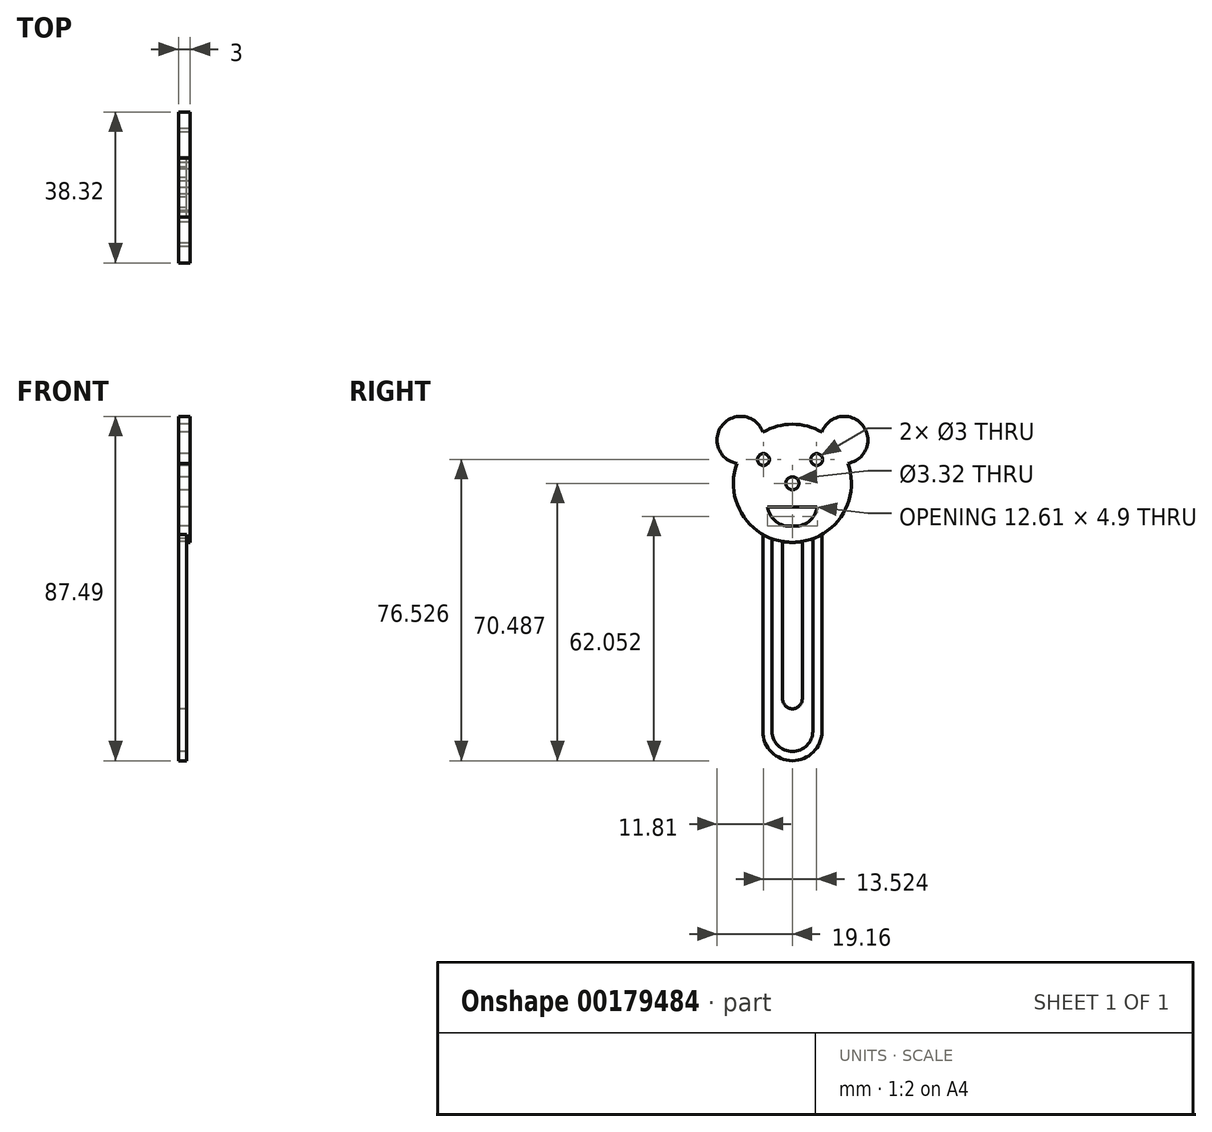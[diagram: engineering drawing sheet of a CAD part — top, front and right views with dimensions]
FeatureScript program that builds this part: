
annotation { "Feature Type Name" : "Feature", "Feature Type Description" : "" }
export const myFeature = defineFeature(function(context is Context, id is Id, definition is map)
    precondition{}
    {
        {
            var Q0;
            Q0=qCreatedBy(makeId("Right.planeOp"),FACE);
            var sketch = newSketch(context, id + "F0", { "sketchPlane" : qUnion([Q0])});
            skCircle(sketch, "E0", {"center": v(0, 41.87) * mm, "radius": 15 * mm});
            skCircle(sketch, "E1", {"center": v(-7.35, 47.9) * mm, "radius": 1.5 * mm});
            skCircle(sketch, "E2", {"center": v(6.17, 47.9) * mm, "radius": 1.5 * mm});
            skCircle(sketch, "E3", {"center": v(0, 41.87) * mm, "radius": 1.66 * mm});
            skArc(sketch, "E4", {"start": v(-8.37, 54.31) * mm, "mid": v(-17, 56.08) * mm, "end": v(-13.73, 47.9) * mm});
            skArc(sketch, "E5", {"start": v(13.73, 47.9) * mm, "mid": v(17, 56.08) * mm, "end": v(8.37, 54.31) * mm});
            skLineSegment(sketch, "E6", {"start": v(-7.5, 28.88) * mm, "end": v(-7.5, -21.12) * mm});
            skLineSegment(sketch, "E7", {"start": v(8.37, 54.31) * mm, "end": v(-40.5, 54.31) * mm, "construction": true});
            skArc(sketch, "E8.0", {"start": v(-7.5, 54.86) * mm, "mid": v(-17.76, 56.72) * mm, "end": v(-14.11, 46.95) * mm});
            skArc(sketch, "E9.0", {"start": v(14.11, 46.95) * mm, "mid": v(17.76, 56.72) * mm, "end": v(7.5, 54.86) * mm});
            skLineSegment(sketch, "E10.MirrorCS", {"start": v(7.5, 28.88) * mm, "end": v(7.5, -21.12) * mm});
            skLineSegment(sketch, "E11.0", {"start": v(-2.5, 27.08) * mm, "end": v(-2.5, -12.92) * mm});
            skLineSegment(sketch, "E12.MirrorCS", {"start": v(2.5, 27.08) * mm, "end": v(2.5, -12.92) * mm});
            skLineSegment(sketch, "E13", {"start": v(0, 35.88) * mm, "end": v(-6.3, 35.88) * mm});
            skArc(sketch, "E14", {"start": v(-6.3, 35.88) * mm, "mid": v(-4.16, 32.15) * mm, "end": v(0, 31.01) * mm});
            skLineSegment(sketch, "E15.MirrorCS", {"start": v(0, 35.88) * mm, "end": v(6.3, 35.88) * mm});
            skArc(sketch, "E16.MirrorCS", {"start": v(6.3, 35.88) * mm, "mid": v(4.16, 32.15) * mm, "end": v(0, 31.01) * mm});
            skArc(sketch, "E17", {"start": v(-2.5, -12.92) * mm, "mid": v(0, -15.42) * mm, "end": v(2.5, -12.92) * mm});
            skLineSegment(sketch, "E18", {"start": v(-5.16, 27.78) * mm, "end": v(-5.16, -21.12) * mm});
            skLineSegment(sketch, "E19.MirrorCS", {"start": v(5.16, 27.78) * mm, "end": v(5.16, -21.12) * mm});
            skArc(sketch, "E20", {"start": v(-5.16, -21.12) * mm, "mid": v(0, -26.28) * mm, "end": v(5.16, -21.12) * mm});
            skArc(sketch, "E21", {"start": v(-7.5, -21.12) * mm, "mid": v(0, -28.62) * mm, "end": v(7.5, -21.12) * mm});
            skSolve(sketch);
        }
        {
            var Q0;
            Q0=makeQuery(id+"F0.imprint","IMPRINT",FACE,{"disambiguationData":[TD([[makeQuery(id+"F0.imprint","IMPRINT",EDGE,{"derivedFrom":sQuery(id+"F0.wireOp",EDGE,"E1")}),-1.0]])]});
            var Q1;
            {var subQ0=sQuery(id+"F0.wireOp",EDGE,"E5");Q1=makeQuery(id+"F0.imprint","IMPRINT",FACE,{"disambiguationData":[TD([[makeQuery(id+"F0.imprint","IMPRINT",EDGE,{"derivedFrom":subQ0}),1.0]])]});}
            var Q2;
            {var subQ0=sQuery(id+"F0.wireOp",EDGE,"E4");Q2=makeQuery(id+"F0.imprint","IMPRINT",FACE,{"disambiguationData":[TD([[makeQuery(id+"F0.imprint","IMPRINT",EDGE,{"derivedFrom":subQ0}),1.0]])]});}
            var Q3;
            {var subQ0=sQuery(id+"F0.wireOp",EDGE,"E5");Q3=makeQuery(id+"F0.imprint","IMPRINT",FACE,{"disambiguationData":[TD([[makeQuery(id+"F0.imprint","IMPRINT",EDGE,{"derivedFrom":subQ0}),-1.0]])]});}
            var Q4;
            {var subQ0=sQuery(id+"F0.wireOp",EDGE,"E4");Q4=makeQuery(id+"F0.imprint","IMPRINT",FACE,{"disambiguationData":[TD([[makeQuery(id+"F0.imprint","IMPRINT",EDGE,{"derivedFrom":subQ0}),-1.0]])]});}
            extrude(context, id + "F1", {"entities" : qUnion([Q0, Q1, Q2, Q3, Q4]), "depth" : 3 * mm});
        }
        {
            var Q0;
            {var subQ0=sQuery(id+"F0.wireOp",EDGE,"E11.0");Q0=makeQuery(id+"F0.imprint","IMPRINT",FACE,{"disambiguationData":[TD([[makeQuery(id+"F0.imprint","IMPRINT",EDGE,{"derivedFrom":subQ0}),1.0]])]});}
            var Q1;
            {var subQ1=sQuery(id+"F0.wireOp",EDGE,"E6");Q1=makeQuery(id+"F0.imprint","IMPRINT",FACE,{"disambiguationData":[TD([[makeQuery(id+"F0.imprint","IMPRINT",EDGE,{"derivedFrom":subQ1}),1.0]])]});}
            extrude(context, id + "F2", {"entities" : qUnion([Q0, Q1]), "operationType" : NewBodyOperationType.ADD, "depth" : 2 * mm});
        }
    });
